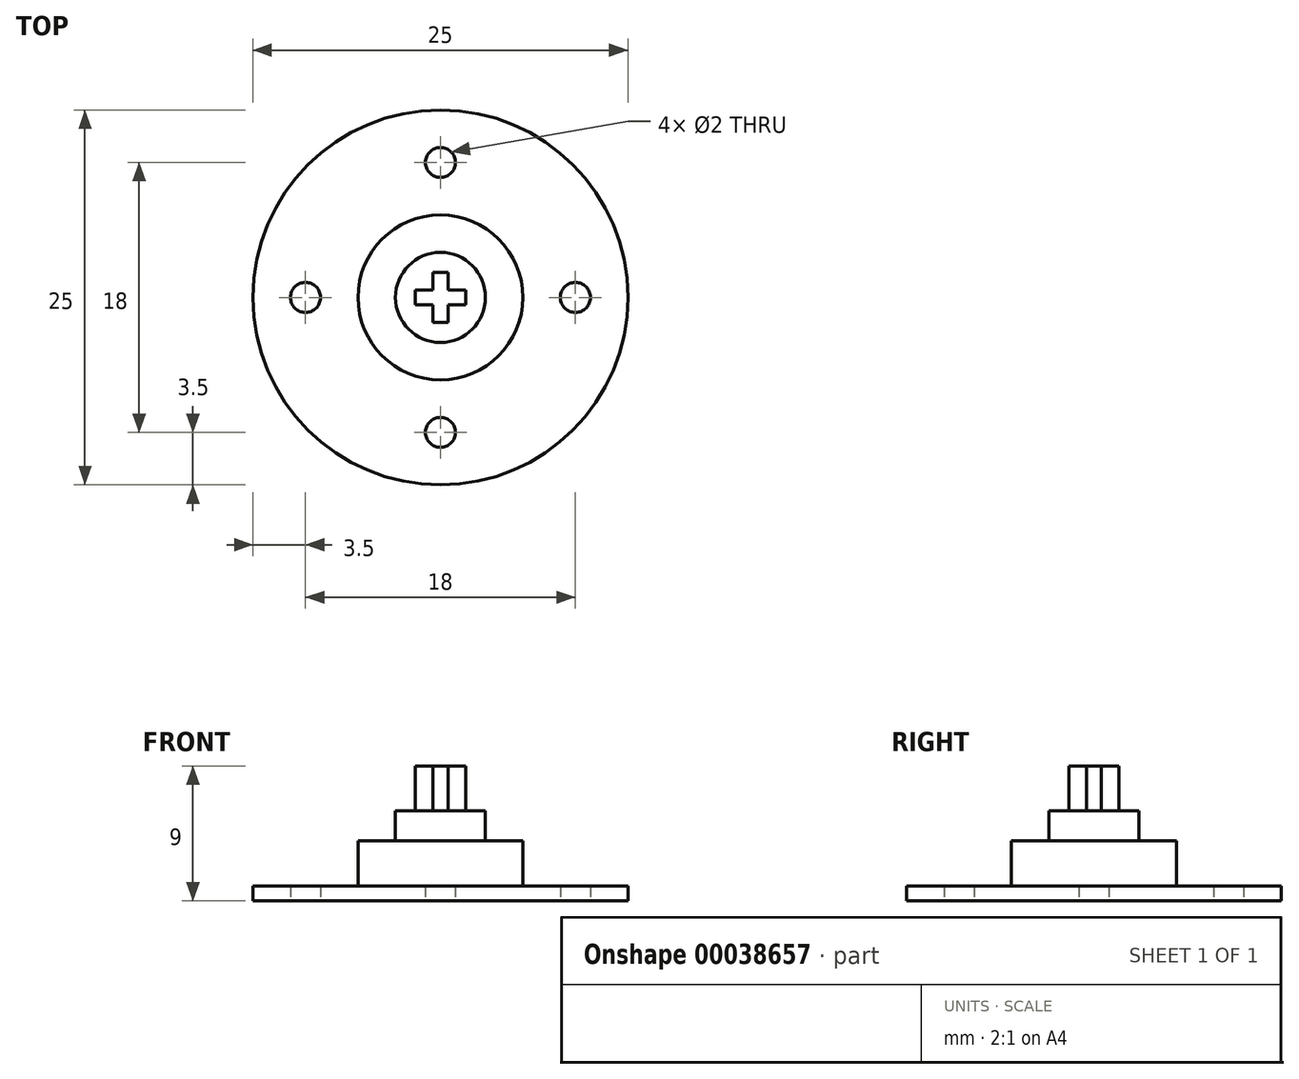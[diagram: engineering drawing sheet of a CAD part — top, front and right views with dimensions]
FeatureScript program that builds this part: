
annotation { "Feature Type Name" : "Feature", "Feature Type Description" : "" }
export const myFeature = defineFeature(function(context is Context, id is Id, definition is map)
    precondition{}
    {
        {
            var Q0;
            Q0=qCreatedBy(makeId("Top.planeOp"),FACE);
            var sketch = newSketch(context, id + "F0", { "sketchPlane" : qUnion([Q0])});
            skCircle(sketch, "E0", {"center": v(0, 0) * mm, "radius": 9 * mm, "construction": true});
            skCircle(sketch, "E1", {"center": v(0, 0) * mm, "radius": 12.5 * mm});
            skCircle(sketch, "E2", {"center": v(0, 9) * mm, "radius": 1 * mm});
            skCircle(sketch, "E3", {"center": v(9, 0) * mm, "radius": 1 * mm});
            skCircle(sketch, "E4", {"center": v(0, -9) * mm, "radius": 1 * mm});
            skCircle(sketch, "E5", {"center": v(-9, 0) * mm, "radius": 1 * mm});
            skSolve(sketch);
        }
        {
            var Q0;
            Q0 = qSketchRegion(id + "F0", true);
            extrude(context, id + "F1", {"entities" : qUnion([Q0]), "depth" : 1 * mm});
        }
        {
            var Q0;
            Q0=makeQuery(id+"F1.opExtrude","CAP_FACE",FACE,{"disambiguationData":[OSD([sQuery(id+"F0.wireOp",EDGE,"E1"),sQuery(id+"F0.wireOp",EDGE,"E2"),sQuery(id+"F0.wireOp",EDGE,"E3"),sQuery(id+"F0.wireOp",EDGE,"E4"),sQuery(id+"F0.wireOp",EDGE,"E5")])],"isStart":false});
            var sketch = newSketch(context, id + "F2", { "sketchPlane" : qUnion([Q0])});
            skCircle(sketch, "E6", {"center": v(0, 0) * mm, "radius": 5.5 * mm});
            skSolve(sketch);
        }
        {
            var Q0;
            Q0 = qSketchRegion(id + "F2", true);
            extrude(context, id + "F3", {"entities" : qUnion([Q0]), "operationType" : NewBodyOperationType.ADD, "depth" : 3 * mm});
        }
        {
            var Q0;
            Q0=makeQuery(id+"F3.opExtrude","CAP_FACE",FACE,{"disambiguationData":[OSD([sQuery(id+"F2.wireOp",EDGE,"E6")])],"isStart":false});
            var sketch = newSketch(context, id + "F4", { "sketchPlane" : qUnion([Q0])});
            skCircle(sketch, "E7", {"center": v(0, 0) * mm, "radius": 3 * mm});
            skSolve(sketch);
        }
        {
            var Q0;
            Q0 = qSketchRegion(id + "F4", true);
            extrude(context, id + "F5", {"entities" : qUnion([Q0]), "operationType" : NewBodyOperationType.ADD, "depth" : 2 * mm});
        }
        {
            var Q0;
            Q0=makeQuery(id+"F5.opExtrude","CAP_FACE",FACE,{"disambiguationData":[OSD([sQuery(id+"F4.wireOp",EDGE,"E7")])],"isStart":false});
            var sketch = newSketch(context, id + "F6", { "sketchPlane" : qUnion([Q0])});
            skCircle(sketch, "E8", {"center": v(0, 0) * mm, "radius": 1.75 * mm, "construction": true});
            skLineSegment(sketch, "E9.bottom", {"start": v(-0.5, 1.68) * mm, "end": v(0.5, 1.68) * mm});
            skLineSegment(sketch, "E9.top", {"start": v(-0.5, -1.68) * mm, "end": v(0.5, -1.68) * mm});
            skLineSegment(sketch, "E9.left", {"start": v(-0.5, 1.68) * mm, "end": v(-0.5, -1.68) * mm});
            skLineSegment(sketch, "E9.right", {"start": v(0.5, 1.68) * mm, "end": v(0.5, -1.68) * mm});
            skLineSegment(sketch, "E10.bottom", {"start": v(-1.68, 0.5) * mm, "end": v(1.68, 0.5) * mm});
            skLineSegment(sketch, "E10.top", {"start": v(-1.68, -0.5) * mm, "end": v(1.68, -0.5) * mm});
            skLineSegment(sketch, "E10.left", {"start": v(-1.68, 0.5) * mm, "end": v(-1.68, -0.5) * mm});
            skLineSegment(sketch, "E10.right", {"start": v(1.68, 0.5) * mm, "end": v(1.68, -0.5) * mm});
            skSolve(sketch);
        }
        {
            var Q0;
            Q0 = qSketchRegion(id + "F6", true);
            extrude(context, id + "F7", {"entities" : qUnion([Q0]), "depth" : 3 * mm});
        }
    });
